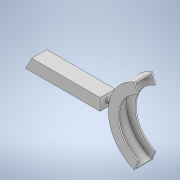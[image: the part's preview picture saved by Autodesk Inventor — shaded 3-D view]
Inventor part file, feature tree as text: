
AUTODESK INVENTOR PART (.ipt)
format: ipt  version: 2021 (Build 250183000, 183)  size: 158,208 bytes
history: native  units: mm
features: extrude x3, sketch x3, plane x1, shell x1, projected_geometry x1
ambient origin geometry x8: Origin, YZ Plane, XZ Plane, XY Plane, X Axis, Y Axis, Z Axis, Center Point
bodies: Solid1 (feature_tree)
feature tree (9):
  extrude  "Extrusion1"  Depth=26.670058mm
  extrude  "Extrusion2"  Depth=8.944mm
  plane  "Work Plane1"
  extrude  "Extrusion3"  Depth=11.775mm
  shell  "Shell1"  Thickness=0.0mm
  sketch  "Sketch2"  dims[d2=136.361055mm d3=26.670058mm]
  sketch  "Sketch3"  dims[d5=0.0mm d6=8.944mm]
  sketch  "Sketch4"  dims[d8=15.0mm d9=11.775mm d11=0.0mm d15=19.753161mm d16=3.486061mm d17=3.714968mm d18=114.810056mm d19=151.780759mm d21=0.0mm d22=2.5mm]
  projected_geometry  "Projected Loop1"
